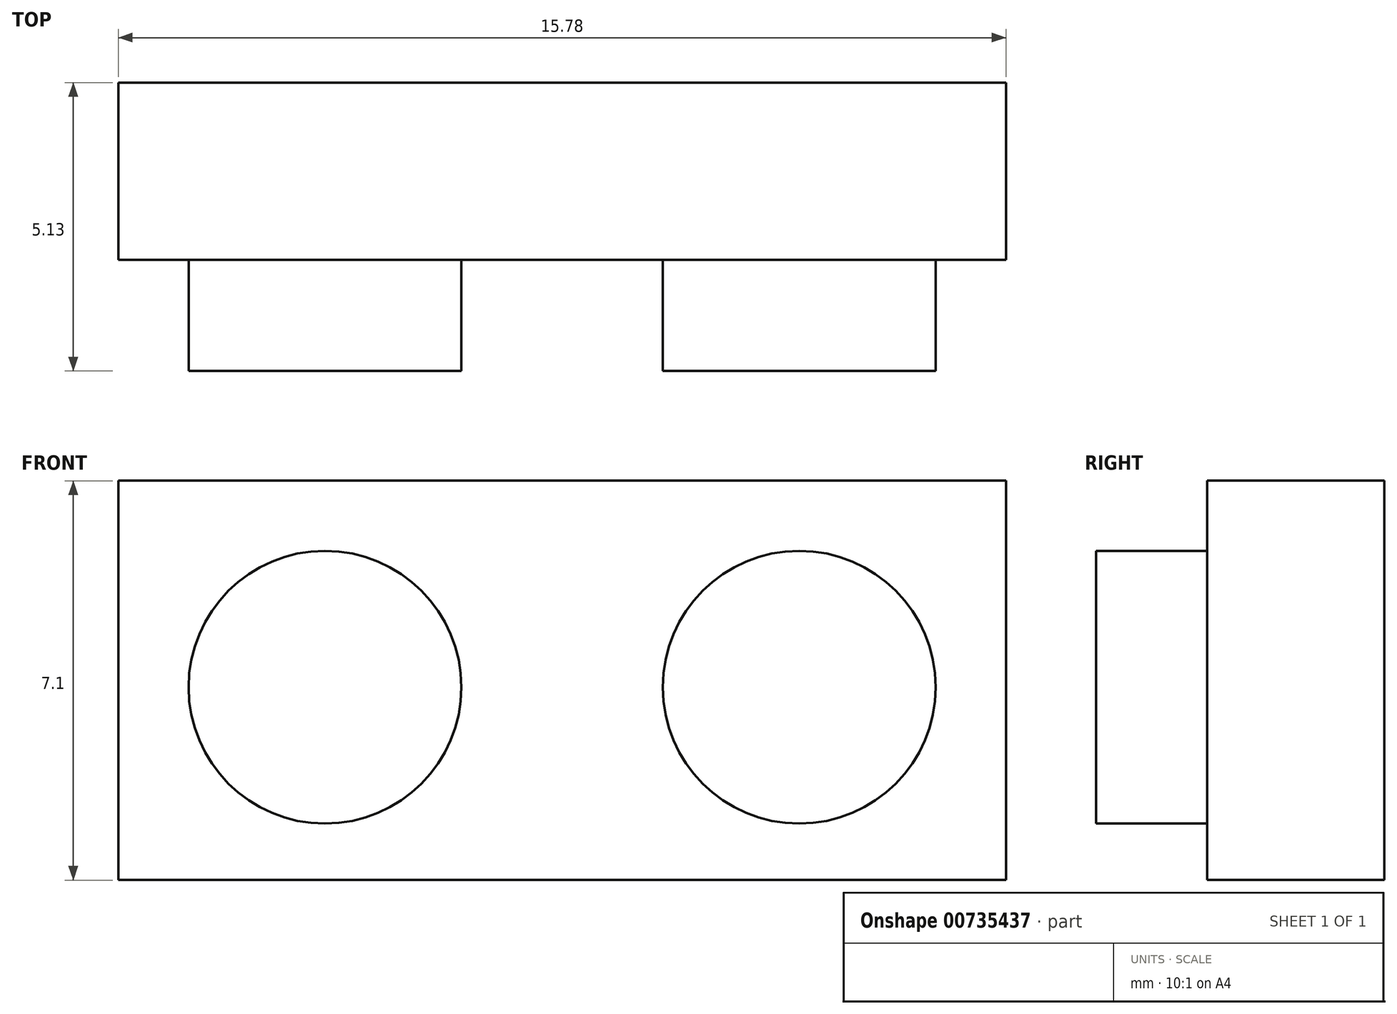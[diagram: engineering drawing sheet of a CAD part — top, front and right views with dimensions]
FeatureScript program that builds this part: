
annotation { "Feature Type Name" : "Feature", "Feature Type Description" : "" }
export const myFeature = defineFeature(function(context is Context, id is Id, definition is map)
    precondition{}
    {
        {
            var Q0;
            Q0=qCreatedBy(makeId("Front.planeOp"),FACE);
            var sketch = newSketch(context, id + "F0", { "sketchPlane" : qUnion([Q0])});
            skLineSegment(sketch, "E0.bottom", {"start": v(-66.46, 18.15) * mm, "end": v(-50.68, 18.15) * mm});
            skLineSegment(sketch, "E0.top", {"start": v(-66.46, 11.05) * mm, "end": v(-50.68, 11.05) * mm});
            skLineSegment(sketch, "E0.left", {"start": v(-50.68, 18.15) * mm, "end": v(-50.68, 11.05) * mm});
            skLineSegment(sketch, "E0.right", {"start": v(-66.46, 18.15) * mm, "end": v(-66.46, 11.05) * mm});
            skSolve(sketch);
        }
        {
            var Q0;
            Q0 = qSketchRegion(id + "F0", true);
            extrude(context, id + "F1", {"entities" : qUnion([Q0]), "depth" : 3.15 * mm, "offsetDistance" : 25 * mm});
        }
        {
            var Q0;
            Q0=makeQuery(id+"F1.opExtrude","CAP_FACE",FACE,{"disambiguationData":[OSD([sQuery(id+"F0.wireOp",EDGE,"E0.bottom"),sQuery(id+"F0.wireOp",EDGE,"E0.top"),sQuery(id+"F0.wireOp",EDGE,"E0.left"),sQuery(id+"F0.wireOp",EDGE,"E0.right")])],"isStart":false});
            var sketch = newSketch(context, id + "F2", { "sketchPlane" : qUnion([Q0])});
            skCircle(sketch, "E1", {"center": v(-62.78, 14.48) * mm, "radius": 2.43 * mm});
            skCircle(sketch, "E2", {"center": v(-54.35, 14.48) * mm, "radius": 2.43 * mm});
            skPoint(sketch, "E3.start.orphan", {"position": v(-62.78, 16.9) * mm});
            skPoint(sketch, "E4.start.orphan", {"position": v(-54.35, 16.9) * mm});
            skPoint(sketch, "E5.start.orphan", {"position": v(-51.93, 14.48) * mm});
            skPoint(sketch, "E6.start.orphan", {"position": v(-65.2, 14.48) * mm});
            skSolve(sketch);
        }
        {
            var Q0;
            Q0 = qSketchRegion(id + "F2", true);
            extrude(context, id + "F3", {"entities" : qUnion([Q0]), "operationType" : NewBodyOperationType.ADD, "depth" : 1.98 * mm, "offsetDistance" : 25 * mm});
        }
    });
